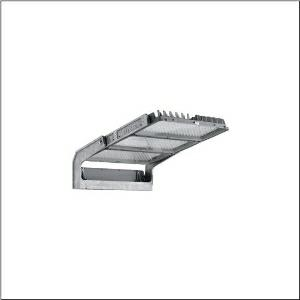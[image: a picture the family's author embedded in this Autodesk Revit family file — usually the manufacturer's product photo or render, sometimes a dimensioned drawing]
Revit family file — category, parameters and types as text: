
# Revit family: floodlight_fl_11_maxi_pro___rs08_5xa779129l01gb_98ff
name_source: partatom
category: Lighting Fixtures
units: mm (PartAtom-declared; Revit-internal decimal feet)

## family parameters
Cut with Voids When Loaded = No
Host = Face
Light Source = No
Part Type = Normal
Room Calculation Point = No
Round Connector Dimension = Use Diameter
Shared = No

## types (1)
- --- (1 x LED, 163120 lm, 1315 W, 5700K)
    Apparent Load = 1315 VA
    CIE Flux Codes = 70 87 98 100 100
    Color Rendering = 70
    Color Temperature = 5700K
    Default Elevation = 1800 mm
    Description = Floodlight FL 11  maxi  pro floodlight; light control with lens of PMMA; cover panel of toughened safety glass, transparent; light distribution: RS08, rotationally symmetric direct distribution, LEDcolour temperature: 5700K, rated luminous flux: 163.120lm, colour rendering: CRI > 70, light colour: 757; luminous efficacy: 124lm/W; brightness control: DALI 2; with terminal, 5-pole, max. 2.5mm², mains connection: 220..240V/380..400V AC, 50/60Hz, surge voltage resistance: line to ground: 10kV, service life up to 100,000h L90. Typical operating time: 1000h per year, ECG replaceable separately, LED unit replaceable without ESD environment, dustproof LED module, dimming range 10..100%; 1315W floodlight with 3x LED unit of diecast aluminium, coated grey; length: 1.003mm / width: 651mm / height: 338mm; mounting bracket, of diecast aluminium, uncoated, natural, protection rating (complete): IP66; insulation class (complete): insulation class I (protective earthing); certification: CE, ENEC, VDE; ball protection: ball impact resistant, only for outdoor installations in the designated locations, permissible operating ambient temperature: -45..+55°C, permissible storage temperature: -40..+85°Cpackaging unit: 1 piece

Light Distribution: RS08
    Height = 320 mm
    Lamp = 1 x LED
    Lamp Light Flux = 163120 lm
    Lamp Power = 1315 W
    Lamp count = 1
    Length = 1002 mm
    Luminous efficacy = 124 lm/W
    Manufacturer = Siteco
    ModVariant = No
    Model = 5XA779129L01GB
    Mounting Place = Ceiling
    Mounting Type = Surface mounted
    Number of Poles = 1
    OnlyDefault = Yes
    Power Factor = 1
    Product Name = Floodlight FL 11 maxi pro | RS08
    Product group = floodlight | ceiling mounted
    ProductGroupID = 301
    Protection Class = Protection class I
    Protection Degree = IP 66
    RLX_Detail_Level = 1
    RLX_Emergency_Light_Flux = 0 lm
    RLX_Emergency_Type = 0
    RLX_Emergency_Type_DB = No
    RlxData = <blob elided: 40085 chars, md5=ed5aa27a>
    Socket = socket
    Standby Power = 0 W
    System Light Flux = 163120 lm
    System Power = 1315 W
    Type Comments = factory setting: luminous flux: 100 % | dim-lin: 254 | 895 mA
    Type Image = l_1356210.jpg
    URL = http://relux.com
    VarID = @adj_024844
    Voltage = 0 V
    Weight = 0.00 kg
    Width = 655 mm

## geometry (parser evidence)
native form markers: Blend x4, Sweep x13
no freeform markers — native parametric forms only
